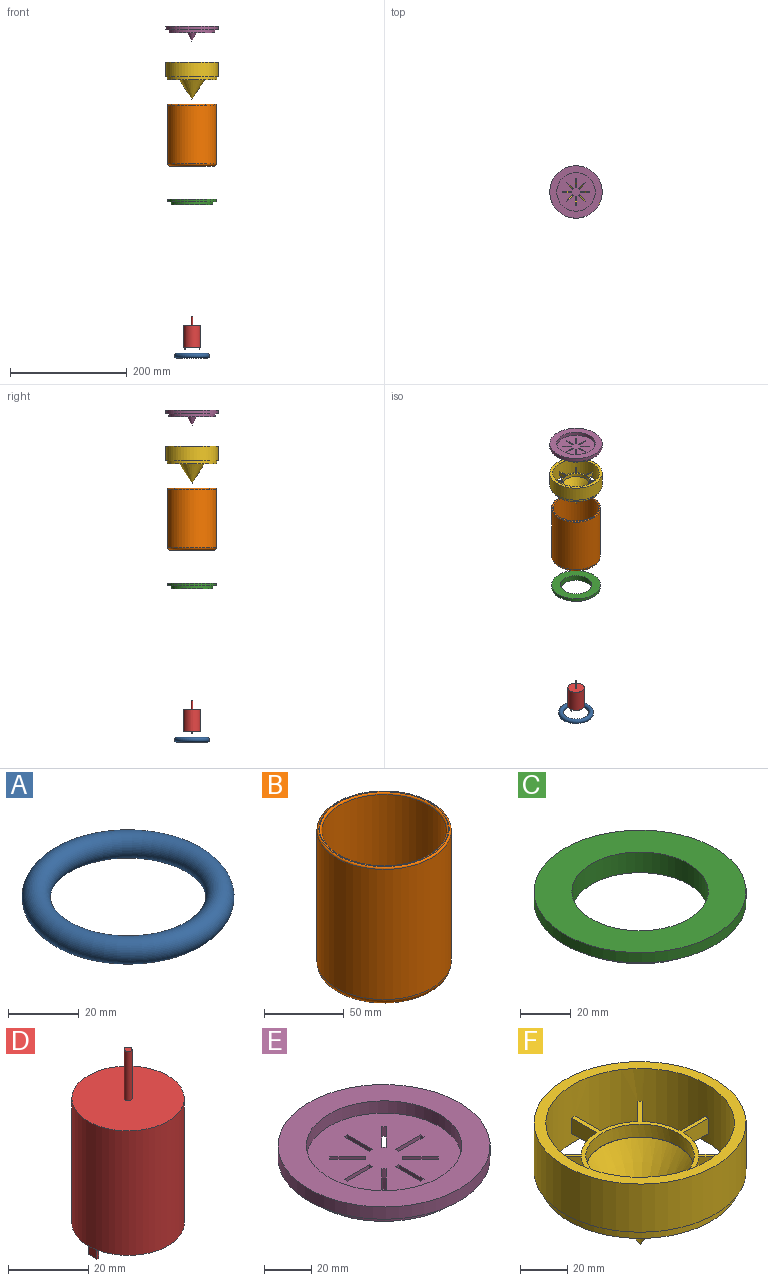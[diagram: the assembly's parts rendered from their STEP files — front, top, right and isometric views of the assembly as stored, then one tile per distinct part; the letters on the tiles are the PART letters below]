
ASSEMBLY  parts=6 mates=2
PART A: 1 faces, bbox 64.9x64.9x8 mm
  f0: torus R=26mm, axis (0,0,1), area 4105.8mm2
PART B: 16 faces, bbox 90.9x90.9x106 mm
  f0: cylinder r=39mm len=96.19mm, axis (0,0,-1), area 23570.8mm2, adj f11,f14
  f1: cylinder r=42mm len=99.65mm, axis (0,0,-1), area 26297mm2, adj f8,f15
  f2: plane 81.46x81.46mm, normal (0,0,1), area 117.1mm2, adj f14,f15
  f3: plane 72.92x72.92mm, normal (0,0,1), area 849.7mm2, adj f10,f11
  f4: cylinder r=27mm len=54mm, axis (0,0,1), area 5030mm2, adj f9,f12
  f5: plane 73.84x73.84mm, normal (0,0,-1), area 1049.2mm2, adj f8,f9
  f6: cylinder r=30mm len=60mm, axis (0,0,-1), area 4936.7mm2, adj f10,f13
  f7: plane 57.46x57.46mm, normal (0,0,1), area 82.4mm2, adj f12,f13
  f8: torus R=36.92mm, axis (0,0,1), area 2013.2mm2, adj f1,f5
  f9: torus R=32.08mm, axis (0,0,1), area 1446.3mm2, adj f4,f5
  f10: torus R=32.54mm, axis (0,0,1), area 775.2mm2, adj f3,f6
  f11: torus R=36.46mm, axis (0,0,1), area 954.5mm2, adj f0,f3
  f12: torus R=28.27mm, axis (0,0,1), area 344.2mm2, adj f4,f7
  f13: torus R=28.73mm, axis (0,0,1), area 370.2mm2, adj f6,f7
  f14: torus R=40.27mm, axis (0,0,1), area 494.6mm2, adj f0,f2
  f15: torus R=40.73mm, axis (0,0,1), area 520.7mm2, adj f1,f2
PART C: 6 faces, bbox 84x84x10 mm
  f0: cylinder r=27mm len=54mm, axis (0,0,-1), area 1696.5mm2, adj f2,f5
  f1: cylinder r=42mm len=84mm, axis (0,0,-1), area 1319.5mm2, adj f2,f3
  f2: plane 84x84mm, normal (0,0,1), area 3251.5mm2, adj f0,f1
  f3: plane 84x84mm, normal (0,0,-1), area 1582.6mm2, adj f1,f4
  f4: cylinder r=35.5mm len=71mm, axis (0,0,1), area 1115.3mm2, adj f3,f5
  f5: plane 71x71mm, normal (0,0,-1), area 1669mm2, adj f0,f4
PART D: 15 faces, bbox 28x28x57 mm
  f0: plane 28x28mm, normal (0,0,-1), area 612.2mm2, adj f1,f5,f6,f7,f8,f10,f11,f12
  f1: cylinder r=14mm len=38mm, axis (0,0,1), area 3342.7mm2, adj f0,f2
  f2: plane 28x28mm, normal (0,0,1), area 612.6mm2, adj f1,f3
  f3: cylinder r=1mm len=15mm, axis (0,0,-1), area 94.2mm2, adj f2,f4
  f4: plane 2x2mm, normal (0,0,1), area 3.1mm2, adj f3
  f5: plane 4x0.6mm, normal (0,1,0), area 2.4mm2, adj f0,f6,f8,f9
  f6: plane 4x3mm, normal (-1,0,0), area 12mm2, adj f0,f5,f7,f9
  f7: plane 4x0.6mm, normal (0,-1,0), area 2.4mm2, adj f0,f6,f8,f9
  f8: plane 4x3mm, normal (1,0,0), area 12mm2, adj f0,f5,f7,f9
  f9: plane 3x0.6mm, normal (0,0,-1), area 1.8mm2, adj f5,f6,f7,f8
  f10: plane 4x0.6mm, normal (0,1,0), area 2.4mm2, adj f0,f11,f13,f14
  f11: plane 4x3mm, normal (-1,0,0), area 12mm2, adj f0,f10,f12,f14
  f12: plane 4x0.6mm, normal (0,-1,0), area 2.4mm2, adj f0,f11,f13,f14
  f13: plane 4x3mm, normal (1,0,0), area 12mm2, adj f0,f10,f12,f14
  f14: plane 3x0.6mm, normal (0,0,-1), area 1.8mm2, adj f10,f11,f12,f13
PART E: 42 faces, bbox 90x90x26.4 mm
  f0: plane 66x66mm, normal (0,0,1), area 3181.2mm2, adj f2,f3,f8,f10,f11,f12,f13,f14
  f1: plane 79x79mm, normal (0,0,-1), area 4460.6mm2, adj f2,f3,f4,f5,f10,f11,f13,f14
  f2: cylinder r=23mm len=5mm, axis (0,0,1), area 10mm2, adj f0,f1,f25,f26
  f3: cylinder r=23mm len=5mm, axis (0,0,1), area 10mm2, adj f0,f1,f10,f11
  f4: cylinder r=39.5mm len=79mm, axis (0,0,1), area 1240.9mm2, adj f1,f6
  f5: cone r=8mm half-angle=28.1deg, axis (0,0,1), area 427.3mm2, adj f1,f12,f16,f20,f24,f27,f31,f35
  f6: plane 90x90mm, normal (0,0,-1), area 1460.1mm2, adj f4,f7
  f7: cylinder r=45mm len=90mm, axis (0,0,-1), area 1795.4mm2, adj f6,f9
  f8: cylinder r=33mm len=66mm, axis (0,0,-1), area 1316.6mm2, adj f0,f9
  f9: plane 90x90mm, normal (0,0,1), area 2940.5mm2, adj f7,f8
  f10: plane 15.04x5mm, normal (0,-1,0), area 75.2mm2, adj f0,f1,f3,f12
  f11: plane 15.04x5mm, normal (0,1,0), area 75.2mm2, adj f0,f1,f3,f12
  f12: cylinder r=8mm len=5mm, axis (0,0,1), area 10mm2, adj f0,f5,f10,f11
  f13: plane 5x1.41mm, normal (0.71,0.71,0), area 10mm2, adj f0,f1,f14,f15
  f14: plane 10.64x10.64mm, normal (0.71,-0.71,0), area 75.2mm2, adj f0,f1,f13,f16
  f15: plane 10.64x10.64mm, normal (-0.71,0.71,0), area 75.2mm2, adj f0,f1,f13,f16
  f16: cylinder r=8mm len=5mm, axis (0,0,1), area 10mm2, adj f0,f5,f14,f15
  f17: plane 5x2mm, normal (0,1,0), area 10mm2, adj f0,f1,f18,f19
  f18: plane 15.04x5mm, normal (1,0,0), area 75.2mm2, adj f0,f1,f17,f20
  f19: plane 15.04x5mm, normal (-1,0,0), area 75.2mm2, adj f0,f1,f17,f20
  f20: cylinder r=8mm len=5mm, axis (0,0,1), area 10mm2, adj f0,f5,f18,f19
  f21: plane 5x1.41mm, normal (-0.71,0.71,0), area 10mm2, adj f0,f1,f22,f23
  f22: plane 10.64x10.64mm, normal (0.71,0.71,0), area 75.2mm2, adj f0,f1,f21,f24
  f23: plane 10.64x10.64mm, normal (-0.71,-0.71,0), area 75.2mm2, adj f0,f1,f21,f24
  f24: cylinder r=8mm len=5mm, axis (0,0,1), area 10mm2, adj f0,f5,f22,f23
  f25: plane 15.04x5mm, normal (0,1,0), area 75.2mm2, adj f0,f1,f2,f27
  f26: plane 15.04x5mm, normal (0,-1,0), area 75.2mm2, adj f0,f1,f2,f27
  f27: cylinder r=8mm len=5mm, axis (0,0,1), area 10mm2, adj f0,f5,f25,f26
  f28: plane 5x1.41mm, normal (-0.71,-0.71,0), area 10mm2, adj f0,f1,f29,f30
  f29: plane 10.64x10.64mm, normal (-0.71,0.71,0), area 75.2mm2, adj f0,f1,f28,f31
  f30: plane 10.64x10.64mm, normal (0.71,-0.71,0), area 75.2mm2, adj f0,f1,f28,f31
  f31: cylinder r=8mm len=5mm, axis (0,0,1), area 10mm2, adj f0,f5,f29,f30
  f32: plane 5x2mm, normal (0,-1,0), area 10mm2, adj f0,f1,f33,f34
  f33: plane 15.04x5mm, normal (-1,0,0), area 75.2mm2, adj f0,f1,f32,f35
  f34: plane 15.04x5mm, normal (1,0,0), area 75.2mm2, adj f0,f1,f32,f35
  f35: cylinder r=8mm len=5mm, axis (0,0,1), area 10mm2, adj f0,f5,f33,f34
  f36: plane 5x1.41mm, normal (0.71,-0.71,0), area 10mm2, adj f0,f1,f37,f38
  f37: plane 10.64x10.64mm, normal (-0.71,-0.71,0), area 75.2mm2, adj f0,f1,f36,f39
  f38: plane 10.64x10.64mm, normal (0.71,0.71,0), area 75.2mm2, adj f0,f1,f36,f39
  f39: cylinder r=8mm len=5mm, axis (0,0,1), area 10mm2, adj f0,f5,f37,f38
  f40: cone r=3.52mm half-angle=28.1deg, axis (0,0,1), area 33.6mm2, adj f41
  f41: plane 4.49x4.49mm, normal (0,0,-1), area 15.8mm2, adj f40
PART F: 43 faces, bbox 90x90x63.1 mm
  f0: plane 12.03x12.03mm, normal (0,0,-1), area 30mm2, adj f20,f32,f33,f38
  f1: plane 15.02x2mm, normal (0,0,-1), area 30mm2, adj f20,f34,f35,f38
  f2: plane 12.03x12.03mm, normal (0,0,-1), area 30mm2, adj f20,f36,f37,f38
  f3: plane 15.02x2mm, normal (0,0,-1), area 30mm2, adj f20,f22,f23,f38
  f4: plane 12.03x12.03mm, normal (0,0,-1), area 30mm2, adj f20,f24,f25,f38
  f5: plane 15.02x2mm, normal (0,0,-1), area 30mm2, adj f20,f26,f27,f38
  f6: plane 12.03x12.03mm, normal (0,0,-1), area 30mm2, adj f20,f28,f29,f38
  f7: plane 15.02x2mm, normal (0,0,-1), area 30mm2, adj f20,f30,f31,f38
  f8: cylinder r=25mm len=15.96mm, axis (0,0,-1), area 141.1mm2, adj f17,f35,f36,f38
  f9: cylinder r=25mm len=15.96mm, axis (0,0,-1), area 141.1mm2, adj f17,f33,f34,f38
  f10: cylinder r=25mm len=15.96mm, axis (0,0,-1), area 141.1mm2, adj f17,f31,f32,f38
  f11: cylinder r=25mm len=15.96mm, axis (0,0,-1), area 141.1mm2, adj f17,f29,f30,f38
  f12: cylinder r=25mm len=15.96mm, axis (0,0,-1), area 141.1mm2, adj f17,f27,f28,f38
  f13: cylinder r=25mm len=15.96mm, axis (0,0,-1), area 141.1mm2, adj f17,f25,f26,f38
  f14: cylinder r=25mm len=15.96mm, axis (0,0,-1), area 141.1mm2, adj f17,f23,f24,f38
  f15: cylinder r=25mm len=15.96mm, axis (0,0,-1), area 141.1mm2, adj f17,f22,f37,f38
  f16: cylinder r=23mm len=46mm, axis (0,0,-1), area 966.5mm2, adj f17,f39
  f17: plane 80x80mm, normal (0,0,1), area 541.6mm2, adj f8,f9,f10,f11,f12,f13,f14,f15
  f18: plane 90x90mm, normal (0,0,-1), area 687.2mm2, adj f19,f41
  f19: cylinder r=45mm len=90mm, axis (0,0,-1), area 7068.6mm2, adj f18,f21
  f20: cylinder r=40mm len=80mm, axis (0,0,-1), area 7411.8mm2, adj f0,f1,f2,f3,f4,f5,f6,f7
  f21: plane 90x90mm, normal (0,0,1), area 1335.2mm2, adj f19,f20
  f22: plane 15.01x8mm, normal (0,1,0), area 120.1mm2, adj f3,f15,f17,f20
  f23: plane 15.01x8mm, normal (0,-1,0), area 120.1mm2, adj f3,f14,f17,f20
  f24: plane 10.61x10.61mm, normal (-0.71,0.71,0), area 120.1mm2, adj f4,f14,f17,f20
  f25: plane 10.61x10.61mm, normal (0.71,-0.71,0), area 120.1mm2, adj f4,f13,f17,f20
  f26: plane 15.01x8mm, normal (-1,0,0), area 120.1mm2, adj f5,f13,f17,f20
  f27: plane 15.01x8mm, normal (1,0,0), area 120.1mm2, adj f5,f12,f17,f20
  f28: plane 10.61x10.61mm, normal (-0.71,-0.71,0), area 120.1mm2, adj f6,f12,f17,f20
  f29: plane 10.61x10.61mm, normal (0.71,0.71,0), area 120.1mm2, adj f6,f11,f17,f20
  f30: plane 15.01x8mm, normal (0,-1,0), area 120.1mm2, adj f7,f11,f17,f20
  f31: plane 15.01x8mm, normal (0,1,0), area 120.1mm2, adj f7,f10,f17,f20
  f32: plane 10.61x10.61mm, normal (0.71,-0.71,0), area 120.1mm2, adj f0,f10,f17,f20
  f33: plane 10.61x10.61mm, normal (-0.71,0.71,0), area 120.1mm2, adj f0,f9,f17,f20
  f34: plane 15.01x8mm, normal (1,0,0), area 120.1mm2, adj f1,f9,f17,f20
  f35: plane 15.01x8mm, normal (-1,0,0), area 120.1mm2, adj f1,f8,f17,f20
  f36: plane 10.61x10.61mm, normal (0.71,0.71,0), area 120.1mm2, adj f2,f8,f17,f20
  f37: plane 10.61x10.61mm, normal (-0.71,-0.71,0), area 120.1mm2, adj f2,f15,f17,f20
  f38: cone r=25mm half-angle=33.3deg, axis (0,0,1), area 3579mm2, adj f0,f1,f2,f3,f4,f5,f6,f7
  f39: cone r=25mm half-angle=56.7deg, axis (0,0,-1), area 21.3mm2, adj f16,f40
  f40: cone r=22.88mm half-angle=33.3deg, axis (0,0,1), area 2996.8mm2, adj f39
  f41: cylinder r=42.5mm len=85mm, axis (0,0,1), area 1335.2mm2, adj f18,f42
  f42: plane 85x85mm, normal (0,0,-1), area 648mm2, adj f20,f41
PLACE A t=(7.02,-17.19,-164.85)mm
PLACE B t=(7.02,-17.19,166.37)mm
PLACE C t=(7.02,-17.19,98.93)mm
PLACE D t=(7.02,-17.19,-112.52)mm
PLACE E t=(7.02,-17.19,394.59)mm
PLACE F t=(7.02,-17.19,313.56)mm
MATE slider E.f4 <-> F.f20  axis (0,0,-1) through (7.02,-17.19,389.59)mm
MATE slider F.f41 <-> B.f0  axis (0,0,-1) through (7.02,-17.19,308.56)mm
